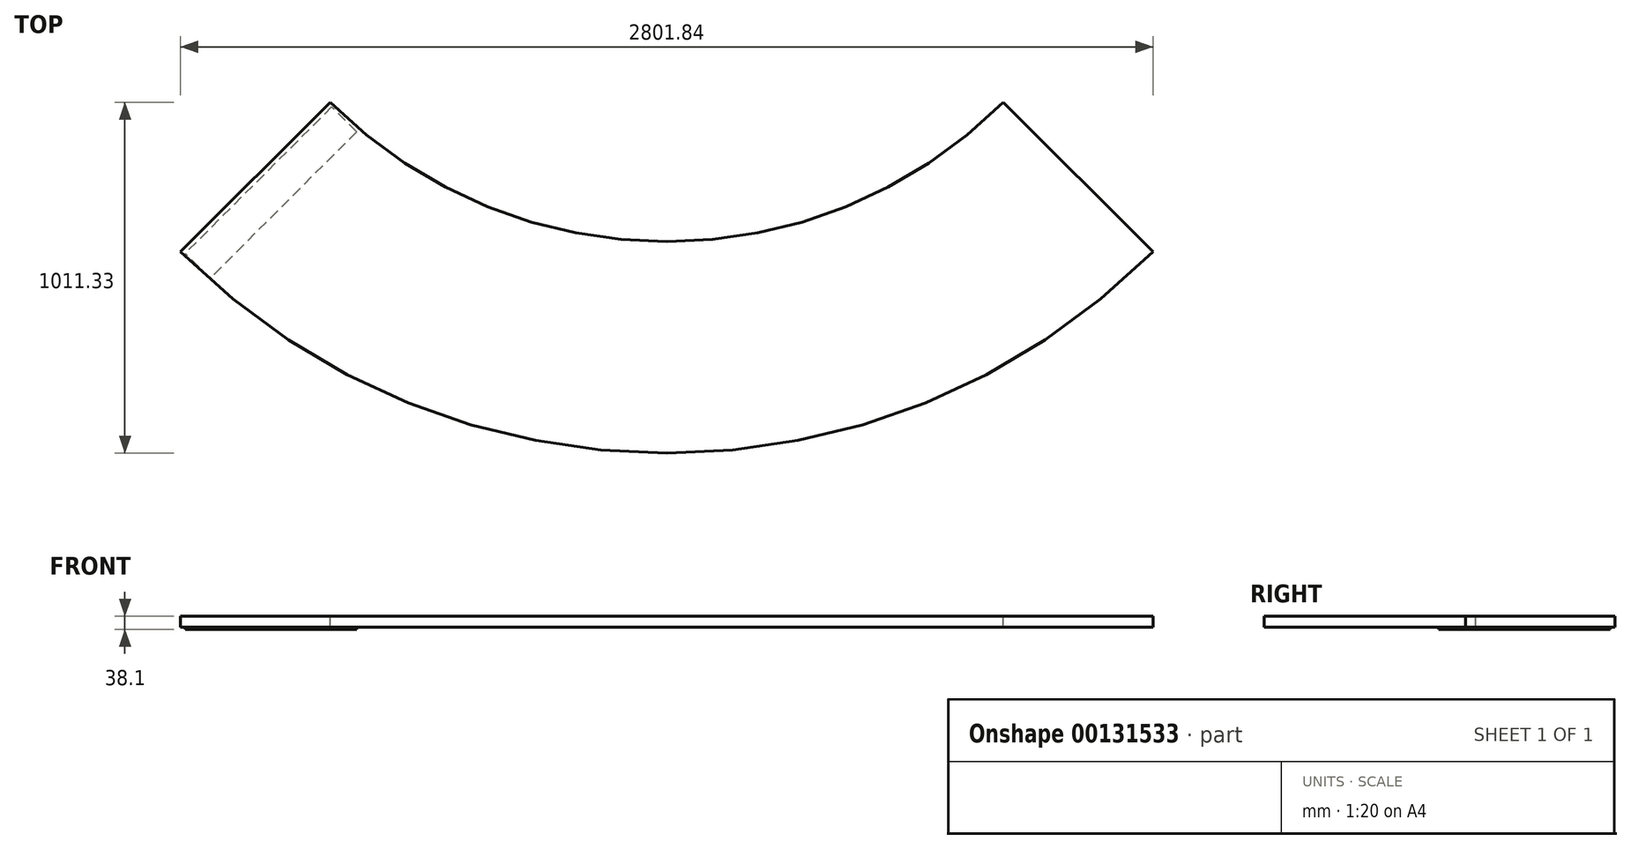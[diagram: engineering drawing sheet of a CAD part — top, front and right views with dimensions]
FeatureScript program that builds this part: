
annotation { "Feature Type Name" : "Feature", "Feature Type Description" : "" }
export const myFeature = defineFeature(function(context is Context, id is Id, definition is map)
    precondition{}
    {
        {
            var Q0;
            Q0=qCreatedBy(makeId("Top.planeOp"),FACE);
            var sketch = newSketch(context, id + "F0", { "sketchPlane" : qUnion([Q0])});
            skArc(sketch, "E0", {"start": v(-969.87, -969.87) * mm, "mid": v(0, -1371.6) * mm, "end": v(969.87, -969.87) * mm});
            skArc(sketch, "E1", {"start": v(-1400.92, -1400.92) * mm, "mid": v(0, -1981.2) * mm, "end": v(1400.92, -1400.92) * mm});
            skLineSegment(sketch, "E2", {"start": v(-969.87, -969.87) * mm, "end": v(-1400.92, -1400.92) * mm});
            skLineSegment(sketch, "E3", {"start": v(969.87, -969.87) * mm, "end": v(1400.92, -1400.92) * mm});
            skLineSegment(sketch, "E4", {"start": v(0, 0) * mm, "end": v(0, -1981.2) * mm, "construction": true});
            skSolve(sketch);
        }
        {
            var Q0;
            Q0=makeQuery(id+"F0.imprint","IMPRINT",FACE,{"disambiguationData":[TD([[makeQuery(id+"F0.imprint","IMPRINT",EDGE,{"derivedFrom":sQuery(id+"F0.wireOp",EDGE,"E0")}),-1.0]])]});
            extrude(context, id + "F1", {"entities" : qUnion([Q0]), "oppositeDirection" : true, "depth" : 31.75 * mm});
        }
        {
            var Q0;
            Q0=makeQuery(id+"F1.opExtrude","CAP_FACE",FACE,{"disambiguationData":[OSD([sQuery(id+"F0.wireOp",EDGE,"E0"),sQuery(id+"F0.wireOp",EDGE,"E1"),sQuery(id+"F0.wireOp",EDGE,"E2"),sQuery(id+"F0.wireOp",EDGE,"E3")])],"isStart":false});
            var sketch = newSketch(context, id + "F2", { "sketchPlane" : qUnion([Q0])});
            skLineSegment(sketch, "E5.0", {"start": v(-969.87, 969.87) * mm, "end": v(-1400.92, 1400.92) * mm, "construction": true});
            skLineSegment(sketch, "E6.0", {"start": v(-965.38, 983.34) * mm, "end": v(-1387.45, 1405.41) * mm});
            skLineSegment(sketch, "E7.0", {"start": v(-893.54, 1055.18) * mm, "end": v(-1315.6, 1477.25) * mm});
            skLineSegment(sketch, "E8", {"start": v(-1104.57, 1266.22) * mm, "end": v(-1176.41, 1194.37) * mm, "construction": true});
            skLineSegment(sketch, "E9.0", {"start": v(-1315.6, 1477.25) * mm, "end": v(-1387.45, 1405.41) * mm});
            skLineSegment(sketch, "E10.0", {"start": v(-893.54, 1055.18) * mm, "end": v(-965.38, 983.34) * mm});
            skPoint(sketch, "E11.orphan", {"position": v(-960.89, 978.85) * mm});
            skPoint(sketch, "E12.orphan", {"position": v(-889.05, 1050.69) * mm});
            skPoint(sketch, "E13.orphan", {"position": v(-1320.1, 1481.74) * mm});
            skPoint(sketch, "E14.orphan", {"position": v(-1391.94, 1409.9) * mm});
            skSolve(sketch);
        }
        {
            var Q0;
            Q0=makeQuery(id+"F2.imprint","IMPRINT",FACE,{"disambiguationData":[TD([[makeQuery(id+"F2.imprint","IMPRINT",EDGE,{"derivedFrom":sQuery(id+"F2.wireOp",EDGE,"E6.0")}),-1.0]])]});
            extrude(context, id + "F3", {"entities" : qUnion([Q0]), "depth" : 6.35 * mm});
        }
    });
